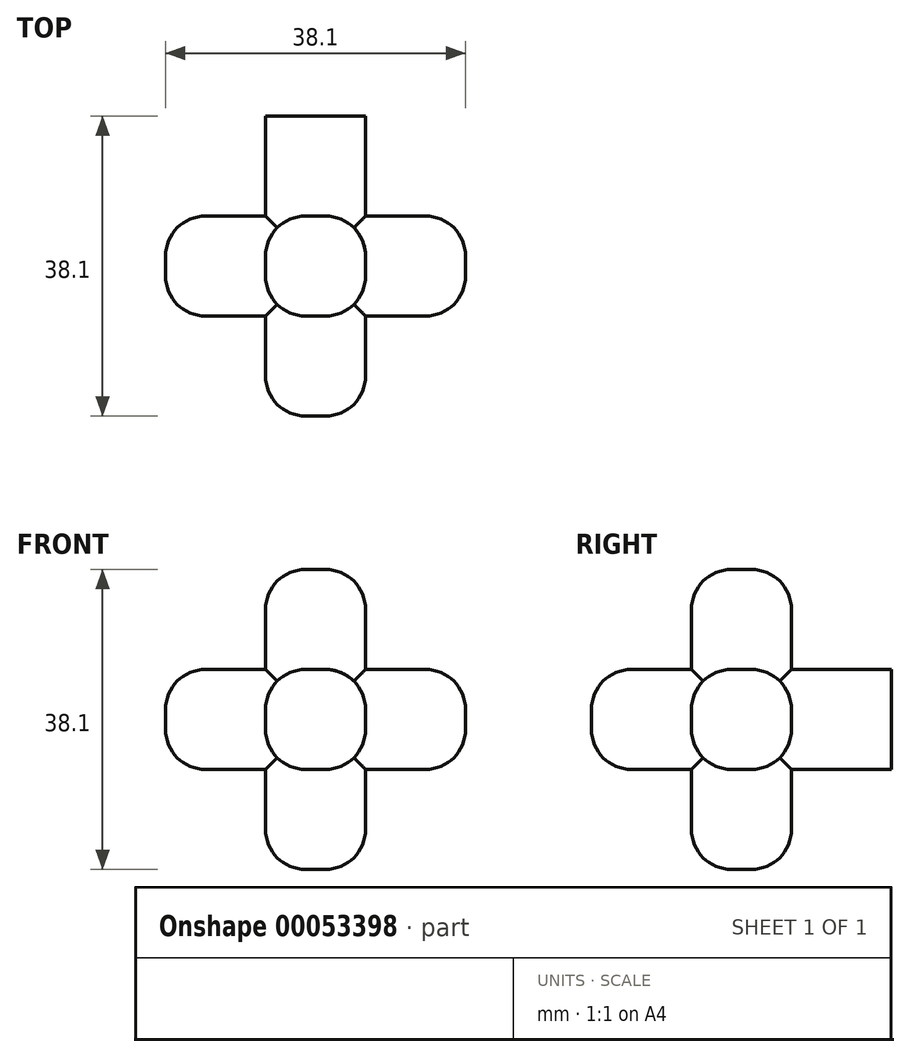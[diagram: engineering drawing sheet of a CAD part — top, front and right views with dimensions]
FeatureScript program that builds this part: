
annotation { "Feature Type Name" : "Feature", "Feature Type Description" : "" }
export const myFeature = defineFeature(function(context is Context, id is Id, definition is map)
    precondition{}
    {
        {
            var Q0;
            Q0=qCreatedBy(makeId("Front.planeOp"),FACE);
            var sketch = newSketch(context, id + "F0", { "sketchPlane" : qUnion([Q0])});
            skLineSegment(sketch, "E0", {"start": v(-30.28, 47.13) * mm, "end": v(-30.28, 34.43) * mm});
            skLineSegment(sketch, "E1", {"start": v(-30.28, 34.43) * mm, "end": v(-17.58, 34.43) * mm});
            skLineSegment(sketch, "E2", {"start": v(-17.58, 34.43) * mm, "end": v(-17.58, 21.73) * mm});
            skLineSegment(sketch, "E3", {"start": v(-17.58, 21.73) * mm, "end": v(-30.28, 21.73) * mm});
            skLineSegment(sketch, "E4", {"start": v(-30.28, 21.73) * mm, "end": v(-30.28, 9.03) * mm});
            skLineSegment(sketch, "E5", {"start": v(-30.28, 9.03) * mm, "end": v(-42.98, 9.03) * mm});
            skLineSegment(sketch, "E6", {"start": v(-42.98, 9.03) * mm, "end": v(-42.98, 21.73) * mm});
            skLineSegment(sketch, "E7", {"start": v(-42.98, 21.73) * mm, "end": v(-55.68, 21.73) * mm});
            skLineSegment(sketch, "E8", {"start": v(-55.68, 21.73) * mm, "end": v(-55.68, 34.43) * mm});
            skLineSegment(sketch, "E9", {"start": v(-55.68, 34.43) * mm, "end": v(-42.98, 34.43) * mm});
            skLineSegment(sketch, "E10", {"start": v(-42.98, 34.43) * mm, "end": v(-42.98, 47.13) * mm});
            skLineSegment(sketch, "E11", {"start": v(-42.98, 47.13) * mm, "end": v(-30.28, 47.13) * mm});
            skSolve(sketch);
        }
        {
            var Q0;
            Q0=makeQuery(id+"F0.imprint","IMPRINT",FACE,{"disambiguationData":[TD([[makeQuery(id+"F0.imprint","IMPRINT",EDGE,{"derivedFrom":sQuery(id+"F0.wireOp",EDGE,"E0")}),-1.0]])]});
            extrude(context, id + "F1", {"entities" : qUnion([Q0]), "depth" : 12.7 * mm});
        }
        {
            var Q0;
            Q0=makeQuery(id+"F1.opExtrude","CAP_FACE",FACE,{"disambiguationData":[OSD([sQuery(id+"F0.wireOp",EDGE,"E0"),sQuery(id+"F0.wireOp",EDGE,"E1"),sQuery(id+"F0.wireOp",EDGE,"E2"),sQuery(id+"F0.wireOp",EDGE,"E3"),sQuery(id+"F0.wireOp",EDGE,"E4"),sQuery(id+"F0.wireOp",EDGE,"E5"),sQuery(id+"F0.wireOp",EDGE,"E6"),sQuery(id+"F0.wireOp",EDGE,"E7"),sQuery(id+"F0.wireOp",EDGE,"E8"),sQuery(id+"F0.wireOp",EDGE,"E9"),sQuery(id+"F0.wireOp",EDGE,"E10"),sQuery(id+"F0.wireOp",EDGE,"E11")])],"isStart":false});
            var sketch = newSketch(context, id + "F2", { "sketchPlane" : qUnion([Q0])});
            skLineSegment(sketch, "E12", {"start": v(-42.98, 34.43) * mm, "end": v(-30.28, 34.43) * mm});
            skLineSegment(sketch, "E13", {"start": v(-30.28, 34.43) * mm, "end": v(-30.28, 21.73) * mm});
            skLineSegment(sketch, "E14", {"start": v(-30.28, 21.73) * mm, "end": v(-42.98, 21.73) * mm});
            skLineSegment(sketch, "E15", {"start": v(-42.98, 21.73) * mm, "end": v(-42.98, 34.43) * mm});
            skSolve(sketch);
        }
        {
            var Q0;
            Q0=makeQuery(id+"F2.imprint","IMPRINT",FACE,{"disambiguationData":[TD([[makeQuery(id+"F2.imprint","IMPRINT",EDGE,{"derivedFrom":sQuery(id+"F2.wireOp",EDGE,"E12")}),-1.0]])]});
            extrude(context, id + "F3", {"entities" : qUnion([Q0]), "operationType" : NewBodyOperationType.ADD, "depth" : 12.7 * mm});
        }
        {
            var Q0;
            Q0=makeQuery(id+"F1.opExtrude","CAP_FACE",FACE,{"disambiguationData":[OSD([sQuery(id+"F0.wireOp",EDGE,"E0"),sQuery(id+"F0.wireOp",EDGE,"E1"),sQuery(id+"F0.wireOp",EDGE,"E2"),sQuery(id+"F0.wireOp",EDGE,"E3"),sQuery(id+"F0.wireOp",EDGE,"E4"),sQuery(id+"F0.wireOp",EDGE,"E5"),sQuery(id+"F0.wireOp",EDGE,"E6"),sQuery(id+"F0.wireOp",EDGE,"E7"),sQuery(id+"F0.wireOp",EDGE,"E8"),sQuery(id+"F0.wireOp",EDGE,"E9"),sQuery(id+"F0.wireOp",EDGE,"E10"),sQuery(id+"F0.wireOp",EDGE,"E11")])],"isStart":true});
            var sketch = newSketch(context, id + "F4", { "sketchPlane" : qUnion([Q0])});
            skLineSegment(sketch, "E16", {"start": v(30.28, 34.43) * mm, "end": v(42.98, 34.43) * mm});
            skLineSegment(sketch, "E17", {"start": v(42.98, 34.43) * mm, "end": v(42.98, 21.73) * mm});
            skLineSegment(sketch, "E18", {"start": v(42.98, 21.73) * mm, "end": v(30.28, 21.73) * mm});
            skLineSegment(sketch, "E19", {"start": v(30.28, 21.73) * mm, "end": v(30.28, 34.43) * mm});
            skSolve(sketch);
        }
        {
            var Q0;
            Q0 = qSketchRegion(id + "F4", true);
            extrude(context, id + "F5", {"entities" : qUnion([Q0]), "operationType" : NewBodyOperationType.ADD, "depth" : 12.7 * mm});
        }
        {
            var Q0;
            Q0=makeQuery(id+"F1.opExtrude","SWEPT_EDGE",EDGE,{"disambiguationData":[OSD([sQuery(id+"F0.wireOp",EDGE,"E10"),sQuery(id+"F0.wireOp",EDGE,"E11")])]});
            var Q1;
            Q1=makeQuery(id+"F1.opExtrude","CAP_EDGE",EDGE,{"disambiguationData":[OSD([sQuery(id+"F0.wireOp",EDGE,"E11")])],"isStart":false});
            var Q2;
            Q2=makeQuery(id+"F1.opExtrude","CAP_EDGE",EDGE,{"disambiguationData":[OSD([sQuery(id+"F0.wireOp",EDGE,"E11")])],"isStart":true});
            var Q3;
            Q3=makeQuery(id+"F1.opExtrude","SWEPT_EDGE",EDGE,{"disambiguationData":[OSD([sQuery(id+"F0.wireOp",EDGE,"E0"),sQuery(id+"F0.wireOp",EDGE,"E11")])]});
            var Q4;
            Q4=makeQuery(id+"F1.opExtrude","CAP_EDGE",EDGE,{"disambiguationData":[OSD([sQuery(id+"F0.wireOp",EDGE,"E10")])],"isStart":false});
            var Q5;
            Q5=makeQuery(id+"F1.opExtrude","CAP_EDGE",EDGE,{"disambiguationData":[OSD([sQuery(id+"F0.wireOp",EDGE,"E0")])],"isStart":false});
            var Q6;
            Q6=makeQuery(id+"F1.opExtrude","CAP_EDGE",EDGE,{"disambiguationData":[OSD([sQuery(id+"F0.wireOp",EDGE,"E0")])],"isStart":true});
            var Q7;
            Q7=makeQuery(id+"F1.opExtrude","CAP_EDGE",EDGE,{"disambiguationData":[OSD([sQuery(id+"F0.wireOp",EDGE,"E10")])],"isStart":true});
            fillet(context, id + "F6", {"entities" : qUnion([Q0, Q1, Q2, Q3, Q4, Q5, Q6, Q7]), "radius" : 5.08 * mm, "tangentPropagation" : true, "allowEdgeOverflow" : false});
        }
        {
            var Q0;
            Q0=makeQuery(id+"F3.opExtrude","SWEPT_EDGE",EDGE,{"disambiguationData":[OSD([sQuery(id+"F0.wireOp",EDGE,"E9"),sQuery(id+"F0.wireOp",EDGE,"E10"),sQuery(id+"F2.wireOp",EDGE,"E12"),sQuery(id+"F2.wireOp",EDGE,"E15")])]});
            var Q1;
            Q1=makeQuery(id+"F3.opExtrude","SWEPT_EDGE",EDGE,{"disambiguationData":[OSD([sQuery(id+"F0.wireOp",EDGE,"E0"),sQuery(id+"F0.wireOp",EDGE,"E1"),sQuery(id+"F2.wireOp",EDGE,"E12"),sQuery(id+"F2.wireOp",EDGE,"E13")])]});
            var Q2;
            Q2=makeQuery(id+"F3.opExtrude","SWEPT_EDGE",EDGE,{"disambiguationData":[OSD([sQuery(id+"F0.wireOp",EDGE,"E6"),sQuery(id+"F0.wireOp",EDGE,"E7"),sQuery(id+"F2.wireOp",EDGE,"E14"),sQuery(id+"F2.wireOp",EDGE,"E15")])]});
            var Q3;
            Q3=makeQuery(id+"F3.opExtrude","SWEPT_EDGE",EDGE,{"disambiguationData":[OSD([sQuery(id+"F0.wireOp",EDGE,"E3"),sQuery(id+"F0.wireOp",EDGE,"E4"),sQuery(id+"F2.wireOp",EDGE,"E13"),sQuery(id+"F2.wireOp",EDGE,"E14")])]});
            var Q4;
            Q4=makeQuery(id+"F3.opExtrude","CAP_EDGE",EDGE,{"disambiguationData":[OSD([sQuery(id+"F2.wireOp",EDGE,"E15")])],"isStart":false});
            var Q5;
            Q5=makeQuery(id+"F3.opExtrude","CAP_EDGE",EDGE,{"disambiguationData":[OSD([sQuery(id+"F2.wireOp",EDGE,"E12")])],"isStart":false});
            var Q6;
            Q6=makeQuery(id+"F3.opExtrude","CAP_EDGE",EDGE,{"disambiguationData":[OSD([sQuery(id+"F2.wireOp",EDGE,"E13")])],"isStart":false});
            var Q7;
            Q7=makeQuery(id+"F3.opExtrude","CAP_EDGE",EDGE,{"disambiguationData":[OSD([sQuery(id+"F2.wireOp",EDGE,"E14")])],"isStart":false});
            fillet(context, id + "F7", {"entities" : qUnion([Q0, Q1, Q2, Q3, Q4, Q5, Q6, Q7]), "radius" : 5.08 * mm, "tangentPropagation" : true, "allowEdgeOverflow" : false});
        }
        {
            var Q0;
            Q0=makeQuery(id+"F1.opExtrude","SWEPT_FACE",FACE,{"disambiguationData":[OSD([sQuery(id+"F0.wireOp",EDGE,"E8")])]});
            var Q1;
            Q1=makeQuery(id+"F1.opExtrude","CAP_EDGE",EDGE,{"disambiguationData":[OSD([sQuery(id+"F0.wireOp",EDGE,"E8")])],"isStart":false});
            var Q2;
            Q2=makeQuery(id+"F1.opExtrude","CAP_EDGE",EDGE,{"disambiguationData":[OSD([sQuery(id+"F0.wireOp",EDGE,"E8")])],"isStart":true});
            var Q3;
            Q3=makeQuery(id+"F1.opExtrude","CAP_EDGE",EDGE,{"disambiguationData":[OSD([sQuery(id+"F0.wireOp",EDGE,"E9")])],"isStart":true});
            var Q4;
            Q4=makeQuery(id+"F1.opExtrude","CAP_EDGE",EDGE,{"disambiguationData":[OSD([sQuery(id+"F0.wireOp",EDGE,"E7")])],"isStart":false});
            var Q5;
            Q5=makeQuery(id+"F1.opExtrude","CAP_EDGE",EDGE,{"disambiguationData":[OSD([sQuery(id+"F0.wireOp",EDGE,"E7")])],"isStart":true});
            var Q6;
            Q6=makeQuery(id+"F1.opExtrude","CAP_EDGE",EDGE,{"disambiguationData":[OSD([sQuery(id+"F0.wireOp",EDGE,"E9")])],"isStart":false});
            fillet(context, id + "F8", {"entities" : qUnion([Q0, Q1, Q2, Q3, Q4, Q5, Q6]), "radius" : 5.08 * mm, "tangentPropagation" : true, "allowEdgeOverflow" : false});
        }
        {
            var Q0;
            Q0=makeQuery(id+"F1.opExtrude","CAP_EDGE",EDGE,{"disambiguationData":[OSD([sQuery(id+"F0.wireOp",EDGE,"E1")])],"isStart":false});
            var Q1;
            Q1=makeQuery(id+"F1.opExtrude","CAP_EDGE",EDGE,{"disambiguationData":[OSD([sQuery(id+"F0.wireOp",EDGE,"E1")])],"isStart":true});
            var Q2;
            Q2=makeQuery(id+"F1.opExtrude","SWEPT_EDGE",EDGE,{"disambiguationData":[OSD([sQuery(id+"F0.wireOp",EDGE,"E1"),sQuery(id+"F0.wireOp",EDGE,"E2")])]});
            var Q3;
            Q3=makeQuery(id+"F1.opExtrude","CAP_EDGE",EDGE,{"disambiguationData":[OSD([sQuery(id+"F0.wireOp",EDGE,"E2")])],"isStart":true});
            var Q4;
            Q4=makeQuery(id+"F1.opExtrude","SWEPT_EDGE",EDGE,{"disambiguationData":[OSD([sQuery(id+"F0.wireOp",EDGE,"E2"),sQuery(id+"F0.wireOp",EDGE,"E3")])]});
            var Q5;
            Q5=makeQuery(id+"F1.opExtrude","CAP_EDGE",EDGE,{"disambiguationData":[OSD([sQuery(id+"F0.wireOp",EDGE,"E2")])],"isStart":false});
            var Q6;
            Q6=makeQuery(id+"F1.opExtrude","CAP_EDGE",EDGE,{"disambiguationData":[OSD([sQuery(id+"F0.wireOp",EDGE,"E3")])],"isStart":false});
            var Q7;
            Q7=makeQuery(id+"F1.opExtrude","CAP_EDGE",EDGE,{"disambiguationData":[OSD([sQuery(id+"F0.wireOp",EDGE,"E3")])],"isStart":true});
            fillet(context, id + "F9", {"entities" : qUnion([Q0, Q1, Q2, Q3, Q4, Q5, Q6, Q7]), "radius" : 5.08 * mm, "tangentPropagation" : true, "allowEdgeOverflow" : false});
        }
        {
            var Q0;
            Q0=makeQuery(id+"F1.opExtrude","CAP_EDGE",EDGE,{"disambiguationData":[OSD([sQuery(id+"F0.wireOp",EDGE,"E6")])],"isStart":true});
            var Q1;
            Q1=makeQuery(id+"F1.opExtrude","CAP_EDGE",EDGE,{"disambiguationData":[OSD([sQuery(id+"F0.wireOp",EDGE,"E6")])],"isStart":false});
            var Q2;
            Q2=makeQuery(id+"F1.opExtrude","CAP_EDGE",EDGE,{"disambiguationData":[OSD([sQuery(id+"F0.wireOp",EDGE,"E4")])],"isStart":false});
            var Q3;
            Q3=makeQuery(id+"F1.opExtrude","CAP_EDGE",EDGE,{"disambiguationData":[OSD([sQuery(id+"F0.wireOp",EDGE,"E4")])],"isStart":true});
            var Q4;
            Q4=makeQuery(id+"F1.opExtrude","SWEPT_EDGE",EDGE,{"disambiguationData":[OSD([sQuery(id+"F0.wireOp",EDGE,"E4"),sQuery(id+"F0.wireOp",EDGE,"E5")])]});
            var Q5;
            Q5=makeQuery(id+"F1.opExtrude","CAP_EDGE",EDGE,{"disambiguationData":[OSD([sQuery(id+"F0.wireOp",EDGE,"E5")])],"isStart":false});
            var Q6;
            Q6=makeQuery(id+"F1.opExtrude","SWEPT_EDGE",EDGE,{"disambiguationData":[OSD([sQuery(id+"F0.wireOp",EDGE,"E5"),sQuery(id+"F0.wireOp",EDGE,"E6")])]});
            var Q7;
            Q7=makeQuery(id+"F1.opExtrude","CAP_EDGE",EDGE,{"disambiguationData":[OSD([sQuery(id+"F0.wireOp",EDGE,"E5")])],"isStart":true});
            fillet(context, id + "F10", {"entities" : qUnion([Q0, Q1, Q2, Q3, Q4, Q5, Q6, Q7]), "radius" : 5.08 * mm, "tangentPropagation" : true, "allowEdgeOverflow" : false});
        }
        {
            var Q0;
            Q0=makeQuery(id+"F5.opExtrude","SWEPT_EDGE",EDGE,{"disambiguationData":[OSD([sQuery(id+"F0.wireOp",EDGE,"E3"),sQuery(id+"F0.wireOp",EDGE,"E4"),sQuery(id+"F4.wireOp",EDGE,"E18"),sQuery(id+"F4.wireOp",EDGE,"E19")])]});
            fillet(context, id + "F11", {"entities" : qUnion([Q0]), "radius" : 5.08 * mm, "tangentPropagation" : true, "allowEdgeOverflow" : false});
        }
        {
            var Q0;
            Q0=makeQuery(id+"F5.opExtrude","SWEPT_EDGE",EDGE,{"disambiguationData":[OSD([sQuery(id+"F0.wireOp",EDGE,"E0"),sQuery(id+"F0.wireOp",EDGE,"E1"),sQuery(id+"F4.wireOp",EDGE,"E16"),sQuery(id+"F4.wireOp",EDGE,"E19")])]});
            var Q1;
            Q1=makeQuery(id+"F5.opExtrude","SWEPT_EDGE",EDGE,{"disambiguationData":[OSD([sQuery(id+"F0.wireOp",EDGE,"E9"),sQuery(id+"F0.wireOp",EDGE,"E10"),sQuery(id+"F4.wireOp",EDGE,"E16"),sQuery(id+"F4.wireOp",EDGE,"E17")])]});
            var Q2;
            Q2=makeQuery(id+"F5.opExtrude","SWEPT_EDGE",EDGE,{"disambiguationData":[OSD([sQuery(id+"F0.wireOp",EDGE,"E6"),sQuery(id+"F0.wireOp",EDGE,"E7"),sQuery(id+"F4.wireOp",EDGE,"E17"),sQuery(id+"F4.wireOp",EDGE,"E18")])]});
            fillet(context, id + "F12", {"entities" : qUnion([Q0, Q1, Q2]), "radius" : 5.08 * mm, "tangentPropagation" : true, "allowEdgeOverflow" : false});
        }
    });
